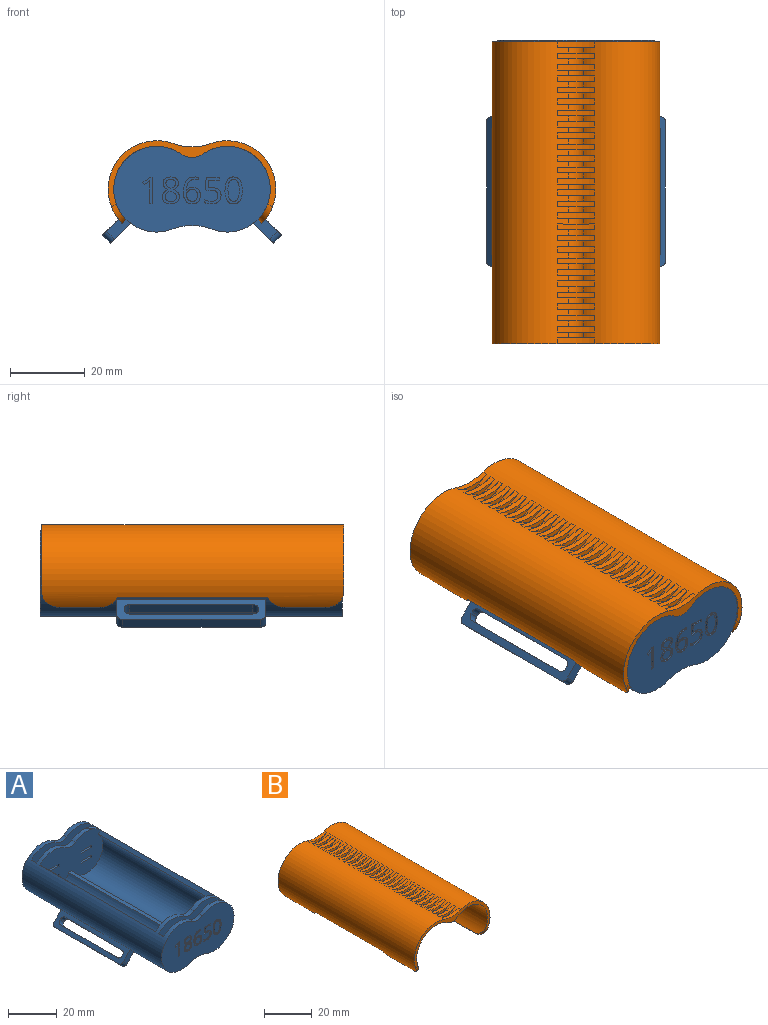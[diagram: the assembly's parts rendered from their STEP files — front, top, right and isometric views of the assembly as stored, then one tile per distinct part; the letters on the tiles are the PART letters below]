
ASSEMBLY  parts=2 mates=1
PART A: 205 faces, bbox 48x81x26 mm
  f0: plane 42x23mm, normal (0,-1,0), area 718.4mm2, adj f3,f9,f52,f88,f89,f90,f91,f92
  f1: plane 40x5.37mm, normal (0.71,0,-0.71), area 175.3mm2, adj f3,f23,f24,f39,f40,f41,f42,f43
  f2: plane 40x5.37mm, normal (-0.71,0,0.71), area 175.3mm2, adj f3,f23,f24,f39,f40,f41,f42,f43
  f3: cylinder r=11.5mm len=81mm, axis (0,1,0), area 2543.9mm2, adj f0,f1,f2,f4,f5,f8,f9,f20
  f4: plane 38x21mm, normal (0,1,0), area 630.6mm2, adj f3,f10,f11,f12,f13,f14,f15,f16
  f5: plane 38x21mm, normal (0,-1,0), area 630.6mm2, adj f3,f6,f7,f8,f10,f11,f12,f13
  f6: plane 67x1.77mm, normal (0,0,1), area 118.3mm2, adj f5,f7,f26,f53
  f7: cylinder r=9.5mm len=67mm, axis (0,1,0), area 2222.9mm2, adj f5,f6,f8,f26
  f8: plane 67x1.41mm, normal (0.71,0,0.71), area 134mm2, adj f3,f5,f7,f26
  f9: cylinder r=15mm len=81mm, axis (0,1,0), area 891mm2, adj f0,f3,f22,f52
  f10: plane 2x1mm, normal (-1,0,0), area 2mm2, adj f4,f5,f11,f13
  f11: plane 6x2mm, normal (0,0,1), area 12mm2, adj f4,f5,f10,f12
  f12: plane 2x1mm, normal (1,0,0), area 2mm2, adj f4,f5,f11,f13
  f13: plane 6x2mm, normal (0,0,-1), area 12mm2, adj f4,f5,f10,f12
  f14: plane 6x2mm, normal (0,0,1), area 12mm2, adj f4,f5,f15,f17
  f15: plane 2x1mm, normal (1,0,0), area 2mm2, adj f4,f5,f14,f16
  f16: plane 6x2mm, normal (0,0,-1), area 12mm2, adj f4,f5,f15,f17
  f17: plane 2x1mm, normal (-1,0,0), area 2mm2, adj f4,f5,f14,f16
  f18: plane 3x1.77mm, normal (0,0,1), area 5.3mm2, adj f4,f19,f21,f63
  f19: cylinder r=9.5mm len=18.12mm, axis (0,-1,0), area 99.5mm2, adj f4,f18,f20,f21
  f20: plane 3x1.41mm, normal (0.71,0,0.71), area 6mm2, adj f3,f4,f19,f21
  f21: plane 38x21mm, normal (0,-1,0), area 641.7mm2, adj f3,f18,f19,f20,f52,f63,f64,f197
  f22: plane 42x23mm, normal (0,1,0), area 797.6mm2, adj f3,f9,f52,f197,f198,f199,f200,f203
  f23: plane 37x2.14mm, normal (-0.71,0,-0.71), area 111.8mm2, adj f1,f2,f48,f49
  f24: plane 6.44x6.44mm, normal (0,1,0), area 18.2mm2, adj f1,f2,f3,f49
  f25: plane 38x21mm, normal (0,-1,0), area 630.6mm2, adj f3,f27,f28,f29,f30,f31,f32,f33
  f26: plane 38x21mm, normal (0,1,0), area 630.6mm2, adj f3,f6,f7,f8,f27,f28,f29,f30
  f27: plane 2x1mm, normal (-1,0,0), area 2mm2, adj f25,f26,f28,f30
  f28: plane 6x2mm, normal (0,0,1), area 12mm2, adj f25,f26,f27,f29
  f29: plane 2x1mm, normal (1,0,0), area 2mm2, adj f25,f26,f28,f30
  f30: plane 6x2mm, normal (0,0,-1), area 12mm2, adj f25,f26,f27,f29
  f31: plane 6x2mm, normal (0,0,1), area 12mm2, adj f25,f26,f32,f34
  f32: plane 2x1mm, normal (1,0,0), area 2mm2, adj f25,f26,f31,f33
  f33: plane 6x2mm, normal (0,0,-1), area 12mm2, adj f25,f26,f32,f34
  f34: plane 2x1mm, normal (-1,0,0), area 2mm2, adj f25,f26,f31,f33
  f35: plane 3x1.77mm, normal (0,0,1), area 5.3mm2, adj f25,f36,f38,f75
  f36: cylinder r=9.5mm len=18.12mm, axis (0,1,0), area 99.5mm2, adj f25,f35,f37,f38
  f37: plane 3x1.41mm, normal (0.71,0,0.71), area 6mm2, adj f3,f25,f36,f38
  f38: plane 38x21mm, normal (0,1,0), area 654.6mm2, adj f3,f35,f36,f37,f52,f75,f76,f202
  f39: plane 6.44x6.44mm, normal (0,-1,0), area 18.2mm2, adj f1,f2,f3,f48
  f40: plane 2.55x2.55mm, normal (0,1,0), area 1.8mm2, adj f1,f2,f44,f47
  f41: plane 33x2.14mm, normal (-0.71,0,-0.71), area 99.7mm2, adj f1,f2,f44,f45
  f42: plane 2.55x2.55mm, normal (0,-1,0), area 1.8mm2, adj f1,f2,f45,f46
  f43: plane 33x2.14mm, normal (0.71,0,0.71), area 99.7mm2, adj f1,f2,f46,f47
  f44: cylinder r=1.5mm len=3.2mm, axis (0.71,0,-0.71), area 7.1mm2, adj f1,f2,f40,f41
  f45: cylinder r=1.5mm len=3.2mm, axis (-0.71,0,0.71), area 7.1mm2, adj f1,f2,f41,f42
  f46: cylinder r=1.5mm len=3.2mm, axis (0.71,0,-0.71), area 7.1mm2, adj f1,f2,f42,f43
  f47: cylinder r=1.5mm len=3.2mm, axis (-0.71,0,0.71), area 7.1mm2, adj f1,f2,f40,f43
  f48: cylinder r=1.5mm len=3.2mm, axis (-0.71,0,0.71), area 7.1mm2, adj f1,f2,f23,f39
  f49: cylinder r=1.5mm len=3.2mm, axis (-0.71,0,0.71), area 7.1mm2, adj f1,f2,f23,f24
  f50: plane 40x5.37mm, normal (-0.71,0,-0.71), area 175.3mm2, adj f52,f65,f66,f77,f78,f79,f80,f81
  f51: plane 40x5.37mm, normal (0.71,0,0.71), area 175.3mm2, adj f52,f65,f66,f77,f78,f79,f80,f81
  f52: cylinder r=11.5mm len=81mm, axis (0,1,0), area 2543.9mm2, adj f0,f4,f5,f9,f21,f22,f25,f26
  f53: cylinder r=9.5mm len=67mm, axis (0,1,0), area 2222.9mm2, adj f5,f6,f26,f54
  f54: plane 67x1.41mm, normal (-0.71,0,0.71), area 134mm2, adj f5,f26,f52,f53
  f55: plane 2x1mm, normal (1,0,0), area 2mm2, adj f4,f5,f56,f58
  f56: plane 6x2mm, normal (0,0,1), area 12mm2, adj f4,f5,f55,f57
  f57: plane 2x1mm, normal (-1,0,0), area 2mm2, adj f4,f5,f56,f58
  f58: plane 6x2mm, normal (0,0,-1), area 12mm2, adj f4,f5,f55,f57
  f59: plane 6x2mm, normal (0,0,1), area 12mm2, adj f4,f5,f60,f62
  f60: plane 2x1mm, normal (-1,0,0), area 2mm2, adj f4,f5,f59,f61
  f61: plane 6x2mm, normal (0,0,-1), area 12mm2, adj f4,f5,f60,f62
  f62: plane 2x1mm, normal (1,0,0), area 2mm2, adj f4,f5,f59,f61
  f63: cylinder r=9.5mm len=18.12mm, axis (0,-1,0), area 99.5mm2, adj f4,f18,f21,f64
  f64: plane 3x1.41mm, normal (-0.71,0,0.71), area 6mm2, adj f4,f21,f52,f63
  f65: plane 37x2.14mm, normal (0.71,0,-0.71), area 111.8mm2, adj f50,f51,f86,f87
  f66: plane 6.44x6.44mm, normal (0,1,0), area 18.2mm2, adj f50,f51,f52,f87
  f67: plane 2x1mm, normal (1,0,0), area 2mm2, adj f25,f26,f68,f70
  f68: plane 6x2mm, normal (0,0,1), area 12mm2, adj f25,f26,f67,f69
  f69: plane 2x1mm, normal (-1,0,0), area 2mm2, adj f25,f26,f68,f70
  f70: plane 6x2mm, normal (0,0,-1), area 12mm2, adj f25,f26,f67,f69
  f71: plane 6x2mm, normal (0,0,1), area 12mm2, adj f25,f26,f72,f74
  f72: plane 2x1mm, normal (-1,0,0), area 2mm2, adj f25,f26,f71,f73
  f73: plane 6x2mm, normal (0,0,-1), area 12mm2, adj f25,f26,f72,f74
  f74: plane 2x1mm, normal (1,0,0), area 2mm2, adj f25,f26,f71,f73
  f75: cylinder r=9.5mm len=18.12mm, axis (0,1,0), area 99.5mm2, adj f25,f35,f38,f76
  f76: plane 3x1.41mm, normal (-0.71,0,0.71), area 6mm2, adj f25,f38,f52,f75
  f77: plane 6.44x6.44mm, normal (0,-1,0), area 18.2mm2, adj f50,f51,f52,f86
  f78: plane 2.55x2.55mm, normal (0,1,0), area 1.8mm2, adj f50,f51,f82,f85
  f79: plane 33x2.14mm, normal (0.71,0,-0.71), area 99.7mm2, adj f50,f51,f82,f83
  f80: plane 2.55x2.55mm, normal (0,-1,0), area 1.8mm2, adj f50,f51,f83,f84
  f81: plane 33x2.14mm, normal (-0.71,0,0.71), area 99.7mm2, adj f50,f51,f84,f85
  f82: cylinder r=1.5mm len=3.2mm, axis (-0.71,0,-0.71), area 7.1mm2, adj f50,f51,f78,f79
  f83: cylinder r=1.5mm len=3.2mm, axis (0.71,0,0.71), area 7.1mm2, adj f50,f51,f79,f80
  f84: cylinder r=1.5mm len=3.2mm, axis (-0.71,0,-0.71), area 7.1mm2, adj f50,f51,f80,f81
  f85: cylinder r=1.5mm len=3.2mm, axis (0.71,0,0.71), area 7.1mm2, adj f50,f51,f78,f81
  f86: cylinder r=1.5mm len=3.2mm, axis (0.71,0,0.71), area 7.1mm2, adj f50,f51,f65,f77
  f87: cylinder r=1.5mm len=3.2mm, axis (0.71,0,0.71), area 7.1mm2, adj f50,f51,f65,f66
  f88: extruded ~1.1x0.5mm, area 0.6mm2, adj f0,f89,f106,f107
  f89: plane 2.11x0.5mm, normal (-1,0,0.08), area 1.1mm2, adj f0,f88,f90,f107
  f90: plane 2.81x0.5mm, normal (0,0,1), area 1.4mm2, adj f0,f89,f91,f107
  f91: plane 0.73x0.5mm, normal (-1,0,0), area 0.4mm2, adj f0,f90,f92,f107
  f92: plane 3.49x0.5mm, normal (0,0,-1), area 1.7mm2, adj f0,f91,f93,f107
  f93: plane 3.28x0.5mm, normal (1,0,-0.08), area 1.6mm2, adj f0,f92,f94,f107
  f94: plane 0.5x0.41mm, normal (0.54,0,0.84), area 0.2mm2, adj f0,f93,f95,f107
  f95: extruded ~1.22x0.5mm, area 0.6mm2, adj f0,f94,f96,f107
  f96: extruded ~1.8x1.47mm, area 1.3mm2, adj f0,f95,f97,f107
  f97: extruded ~1.15x0.5mm, area 0.6mm2, adj f0,f96,f98,f107
  f98: extruded ~1.31x0.5mm, area 0.7mm2, adj f0,f97,f99,f107
  f99: extruded ~0.98x0.5mm, area 0.5mm2, adj f0,f98,f100,f107
  f100: extruded ~0.83x0.5mm, area 0.5mm2, adj f0,f99,f101,f107
  f101: plane 0.77x0.5mm, normal (1,0,0), area 0.4mm2, adj f0,f100,f102,f107
  f102: extruded ~1.81x0.5mm, area 0.9mm2, adj f0,f101,f103,f107
  f103: extruded ~1.91x0.62mm, area 1mm2, adj f0,f102,f104,f107
  f104: extruded ~1.71x0.69mm, area 1mm2, adj f0,f103,f105,f107
  f105: extruded ~1.5x0.64mm, area 0.8mm2, adj f0,f104,f106,f107
  f106: extruded ~1.74x0.55mm, area 0.9mm2, adj f0,f88,f105,f107
  f107: plane 7.11x4.41mm, normal (0,-1,0), area 11.4mm2, adj f88,f89,f90,f91,f92,f93,f94,f95
  f108: extruded ~2.28x0.64mm, area 1.2mm2, adj f0,f109,f132,f133
  f109: extruded ~1.73x0.82mm, area 1mm2, adj f0,f108,f110,f133
  f110: extruded ~1.61x0.63mm, area 0.9mm2, adj f0,f109,f111,f133
  f111: extruded ~1.72x0.6mm, area 0.9mm2, adj f0,f110,f112,f133
  f112: extruded ~1.55x0.54mm, area 0.8mm2, adj f0,f111,f113,f133
  f113: extruded ~1.49x0.57mm, area 0.8mm2, adj f0,f112,f114,f133
  f114: extruded ~1.67x0.83mm, area 1mm2, adj f0,f113,f115,f133
  f115: plane 0.5x0.06mm, normal (0,0,-1), area 0mm2, adj f0,f114,f116,f133
  f116: extruded ~2.21x0.65mm, area 1.2mm2, adj f0,f115,f117,f133
  f117: extruded ~1.72x0.7mm, area 1mm2, adj f0,f116,f118,f133
  f118: extruded ~0.84x0.5mm, area 0.4mm2, adj f0,f117,f119,f133
  f119: plane 0.69x0.5mm, normal (-1,0,0), area 0.3mm2, adj f0,f118,f120,f133
  f120: extruded ~0.85x0.5mm, area 0.4mm2, adj f0,f119,f121,f133
  f121: extruded ~2.38x1.02mm, area 1.3mm2, adj f0,f120,f132,f133
  f122: extruded ~0.8x0.5mm, area 0.4mm2, adj f123,f131,f133,f134
  f123: extruded ~0.68x0.54mm, area 0.4mm2, adj f122,f124,f133,f134
  f124: extruded ~0.92x0.5mm, area 0.5mm2, adj f123,f125,f133,f134
  f125: extruded ~0.65x0.5mm, area 0.3mm2, adj f124,f126,f133,f134
  f126: extruded ~0.57x0.5mm, area 0.4mm2, adj f125,f127,f133,f134
  f127: extruded ~0.79x0.5mm, area 0.4mm2, adj f126,f128,f133,f134
  f128: extruded ~1.05x0.5mm, area 0.6mm2, adj f127,f129,f133,f134
  f129: extruded ~1.09x0.5mm, area 0.6mm2, adj f128,f130,f133,f134
  f130: extruded ~1.24x0.5mm, area 0.7mm2, adj f129,f131,f133,f134
  f131: extruded ~1.06x0.5mm, area 0.6mm2, adj f122,f130,f133,f134
  f132: extruded ~3.09x0.8mm, area 1.6mm2, adj f0,f108,f121,f133
  f133: plane 7.21x4.58mm, normal (0,-1,0), area 12.7mm2, adj f108,f109,f110,f111,f112,f113,f114,f115
  f134: plane 3.16x2.97mm, normal (0,-1,0), area 7.6mm2, adj f122,f123,f124,f125,f126,f127,f128,f129
  f135: extruded ~2.68x0.59mm, area 1.4mm2, adj f0,f136,f150,f151
  f136: extruded ~1.73x0.93mm, area 1mm2, adj f0,f135,f137,f151
  f137: extruded ~1.74x0.89mm, area 1mm2, adj f0,f136,f138,f151
  f138: extruded ~2.72x0.57mm, area 1.4mm2, adj f0,f137,f139,f151
  f139: extruded ~2.69x0.59mm, area 1.4mm2, adj f0,f138,f140,f151
  f140: extruded ~1.72x0.92mm, area 1mm2, adj f0,f139,f141,f151
  f141: extruded ~1.75x0.9mm, area 1mm2, adj f0,f140,f150,f151
  f142: extruded ~2.22x0.5mm, area 1.1mm2, adj f143,f149,f151,f152
  f143: extruded ~1.15x0.69mm, area 0.7mm2, adj f142,f144,f151,f152
  f144: extruded ~1.15x0.7mm, area 0.7mm2, adj f143,f145,f151,f152
  f145: extruded ~2.21x0.5mm, area 1.1mm2, adj f144,f146,f151,f152
  f146: extruded ~2.22x0.5mm, area 1.1mm2, adj f145,f147,f151,f152
  f147: extruded ~1.15x0.71mm, area 0.7mm2, adj f146,f148,f151,f152
  f148: extruded ~1.15x0.7mm, area 0.7mm2, adj f147,f149,f151,f152
  f149: extruded ~2.23x0.5mm, area 1.1mm2, adj f142,f148,f151,f152
  f150: extruded ~2.72x0.57mm, area 1.4mm2, adj f0,f135,f141,f151
  f151: plane 7.22x4.64mm, normal (0,-1,0), area 13mm2, adj f135,f136,f137,f138,f139,f140,f141,f142
  f152: plane 5.84x3.02mm, normal (0,-1,0), area 14.9mm2, adj f142,f143,f144,f145,f146,f147,f148,f149
  f153: extruded ~1.51x0.5mm, area 0.8mm2, adj f0,f154,f183,f184
  f154: extruded ~1.22x0.56mm, area 0.7mm2, adj f0,f153,f155,f184
  f155: extruded ~0.97x0.5mm, area 0.5mm2, adj f0,f154,f156,f184
  f156: extruded ~0.95x0.81mm, area 0.6mm2, adj f0,f155,f157,f184
  f157: extruded ~1.88x1.47mm, area 1.3mm2, adj f0,f156,f158,f184
  f158: extruded ~1.39x0.6mm, area 0.8mm2, adj f0,f157,f159,f184
  f159: extruded ~1.73x0.5mm, area 0.9mm2, adj f0,f158,f160,f184
  f160: extruded ~1.67x0.52mm, area 0.9mm2, adj f0,f159,f161,f184
  f161: extruded ~1.39x0.61mm, area 0.8mm2, adj f0,f160,f162,f184
  f162: extruded ~1.04x0.5mm, area 0.6mm2, adj f0,f161,f163,f184
  f163: extruded ~1.21x0.86mm, area 0.7mm2, adj f0,f162,f164,f184
  f164: extruded ~1.03x0.78mm, area 0.6mm2, adj f0,f163,f165,f184
  f165: extruded ~0.95x0.5mm, area 0.5mm2, adj f0,f164,f166,f184
  f166: extruded ~1.23x0.56mm, area 0.7mm2, adj f0,f165,f183,f184
  f167: extruded ~0.89x0.5mm, area 0.5mm2, adj f168,f181,f184,f186
  f168: extruded ~1.04x0.68mm, area 0.6mm2, adj f167,f169,f184,f186
  f169: extruded ~1.3x0.7mm, area 0.7mm2, adj f168,f170,f184,f186
  f170: extruded ~0.83x0.5mm, area 0.5mm2, adj f169,f171,f184,f186
  f171: extruded ~0.92x0.5mm, area 0.5mm2, adj f170,f172,f184,f186
  f172: extruded ~1.11x0.5mm, area 0.6mm2, adj f171,f173,f184,f186
  f173: extruded ~1.12x0.5mm, area 0.6mm2, adj f172,f181,f184,f186
  f174: extruded ~0.96x0.5mm, area 0.5mm2, adj f175,f182,f184,f185
  f175: extruded ~0.77x0.5mm, area 0.4mm2, adj f174,f176,f184,f185
  f176: extruded ~0.77x0.5mm, area 0.4mm2, adj f175,f177,f184,f185
  f177: extruded ~0.97x0.62mm, area 0.6mm2, adj f176,f178,f184,f185
  f178: extruded ~1.05x0.63mm, area 0.6mm2, adj f177,f179,f184,f185
  f179: extruded ~0.76x0.5mm, area 0.4mm2, adj f178,f180,f184,f185
  f180: extruded ~0.77x0.5mm, area 0.4mm2, adj f179,f182,f184,f185
  f181: extruded ~0.9x0.5mm, area 0.5mm2, adj f167,f173,f184,f186
  f182: extruded ~0.94x0.5mm, area 0.5mm2, adj f174,f180,f184,f185
  f183: extruded ~1.52x0.5mm, area 0.8mm2, adj f0,f153,f166,f184
  f184: plane 7.21x4.61mm, normal (0,-1,0), area 14.6mm2, adj f153,f154,f155,f156,f157,f158,f159,f160
  f185: plane 2.59x2.45mm, normal (0,-1,0), area 4.8mm2, adj f174,f175,f176,f177,f178,f179,f180,f182
  f186: plane 3.04x2.79mm, normal (0,-1,0), area 6.4mm2, adj f167,f168,f169,f170,f171,f172,f173,f181
  f187: plane 7.01x0.5mm, normal (-1,0,0), area 3.5mm2, adj f0,f188,f195,f196
  f188: plane 0.67x0.5mm, normal (0,0,-1), area 0.3mm2, adj f0,f187,f189,f196
  f189: plane 1.86x1.44mm, normal (0.61,0,-0.79), area 1.2mm2, adj f0,f188,f190,f196
  f190: plane 0.55x0.5mm, normal (0.79,0,0.61), area 0.3mm2, adj f0,f189,f191,f196
  f191: extruded ~1.14x0.94mm, area 0.7mm2, adj f0,f190,f192,f196
  f192: extruded ~0.5x0.23mm, area 0.2mm2, adj f0,f191,f193,f196
  f193: extruded ~1.18x0.5mm, area 0.6mm2, adj f0,f192,f194,f196
  f194: plane 5x0.5mm, normal (1,0,0), area 2.5mm2, adj f0,f193,f195,f196
  f195: plane 0.78x0.5mm, normal (0,0,1), area 0.4mm2, adj f0,f187,f194,f196
  f196: plane 7.01x2.53mm, normal (0,-1,0), area 6.7mm2, adj f187,f188,f189,f190,f191,f192,f193,f194
  f197: cylinder r=1.5mm len=3mm, axis (0,1,0), area 10.4mm2, adj f21,f22,f199,f200
  f198: cylinder r=1.5mm len=3mm, axis (0,1,0), area 10.4mm2, adj f21,f22,f199,f200
  f199: cylinder r=5mm len=2mm, axis (0,1,0), area 3.1mm2, adj f21,f22,f197,f198
  f200: cylinder r=5mm len=2mm, axis (0,1,0), area 3.1mm2, adj f21,f22,f197,f198
  f201: cylinder r=5mm len=5.76mm, axis (0,-1,0), area 12.3mm2, adj f3,f25,f26,f52
  f202: cylinder r=5mm len=5.76mm, axis (0,-1,0), area 12.3mm2, adj f0,f3,f38,f52
  f203: cylinder r=5mm len=5.76mm, axis (0,1,0), area 12.3mm2, adj f3,f21,f22,f52
  f204: cylinder r=5mm len=5.76mm, axis (0,1,0), area 12.3mm2, adj f3,f4,f5,f52
PART B: 126 faces, bbox 45x81x23.1 mm
  f0: plane 10.6x1.06mm, normal (-0.71,0,-0.71), area 15.8mm2, adj f1,f34,f118,f121
  f1: cylinder r=13mm len=80.94mm, axis (0,1,0), area 2827.1mm2, adj f0,f2,f3,f4,f5,f6,f7,f8
  f2: cylinder r=3.5mm len=4.03mm, axis (0,1,0), area 6.7mm2, adj f1,f28,f113,f117
  f3: cylinder r=3.5mm len=4.03mm, axis (0,1,0), area 6.7mm2, adj f1,f28,f110,f114
  f4: cylinder r=3.5mm len=4.03mm, axis (0,1,0), area 6.7mm2, adj f1,f28,f107,f111
  f5: cylinder r=3.5mm len=4.03mm, axis (0,1,0), area 6.7mm2, adj f1,f28,f104,f108
  f6: cylinder r=3.5mm len=4.03mm, axis (0,1,0), area 6.7mm2, adj f1,f28,f101,f105
  f7: cylinder r=3.5mm len=4.03mm, axis (0,1,0), area 6.7mm2, adj f1,f28,f98,f102
  f8: cylinder r=3.5mm len=4.03mm, axis (0,1,0), area 6.7mm2, adj f1,f28,f95,f99
  f9: cylinder r=3.5mm len=4.03mm, axis (0,1,0), area 6.7mm2, adj f1,f28,f92,f96
  f10: cylinder r=3.5mm len=4.03mm, axis (0,1,0), area 6.7mm2, adj f1,f28,f89,f93
  f11: cylinder r=3.5mm len=4.03mm, axis (0,1,0), area 6.7mm2, adj f1,f28,f86,f90
  f12: cylinder r=3.5mm len=4.03mm, axis (0,1,0), area 6.7mm2, adj f1,f28,f83,f87
  f13: cylinder r=3.5mm len=4.03mm, axis (0,1,0), area 6.7mm2, adj f1,f28,f80,f84
  f14: cylinder r=3.5mm len=4.03mm, axis (0,1,0), area 6.7mm2, adj f1,f28,f77,f81
  f15: cylinder r=3.5mm len=4.03mm, axis (0,1,0), area 6.7mm2, adj f1,f28,f74,f78
  f16: cylinder r=3.5mm len=4.03mm, axis (0,1,0), area 6.7mm2, adj f1,f28,f71,f75
  f17: cylinder r=3.5mm len=4.03mm, axis (0,1,0), area 6.7mm2, adj f1,f28,f68,f72
  f18: cylinder r=3.5mm len=4.03mm, axis (0,1,0), area 6.7mm2, adj f1,f28,f65,f69
  f19: cylinder r=3.5mm len=4.03mm, axis (0,1,0), area 6.7mm2, adj f1,f28,f62,f66
  f20: cylinder r=3.5mm len=4.03mm, axis (0,1,0), area 6.7mm2, adj f1,f28,f59,f63
  f21: cylinder r=3.5mm len=4.03mm, axis (0,1,0), area 6.7mm2, adj f1,f28,f56,f60
  f22: cylinder r=3.5mm len=4.03mm, axis (0,1,0), area 6.7mm2, adj f1,f28,f53,f57
  f23: cylinder r=3.5mm len=4.03mm, axis (0,1,0), area 6.7mm2, adj f1,f28,f50,f54
  f24: cylinder r=3.5mm len=4.03mm, axis (0,1,0), area 6.7mm2, adj f1,f28,f47,f51
  f25: cylinder r=3.5mm len=4.03mm, axis (0,1,0), area 6.7mm2, adj f1,f28,f44,f48
  f26: cylinder r=3.5mm len=4.03mm, axis (0,1,0), area 6.7mm2, adj f1,f28,f41,f45
  f27: cylinder r=3.5mm len=4.03mm, axis (0,1,0), area 6.7mm2, adj f1,f28,f39,f42
  f28: cylinder r=13mm len=80.94mm, axis (0,1,0), area 2827.1mm2, adj f2,f3,f4,f5,f6,f7,f8,f9
  f29: cylinder r=11.5mm len=80.94mm, axis (0,1,0), area 2602.9mm2, adj f30,f31,f32,f33,f37,f116,f119,f120
  f30: cylinder r=5mm len=80.94mm, axis (0,1,0), area 496.6mm2, adj f29,f32,f34,f116
  f31: plane 10.66x1.06mm, normal (0.71,0,-0.71), area 15.9mm2, adj f28,f29,f124,f125
  f32: plane 45x17.95mm, normal (0,-1,0), area 108mm2, adj f1,f28,f29,f30,f34,f38,f123,f125
  f33: plane 40.42x1.32mm, normal (0.5,0,-0.87), area 60.6mm2, adj f28,f29,f120,f124
  f34: cylinder r=11.5mm len=80.94mm, axis (0,1,0), area 2602.9mm2, adj f0,f30,f32,f35,f36,f116,f118,f121
  f35: plane 10.66x1.06mm, normal (-0.71,0,-0.71), area 15.9mm2, adj f1,f34,f122,f123
  f36: plane 40.42x1.32mm, normal (-0.5,0,-0.87), area 60.6mm2, adj f1,f34,f121,f122
  f37: plane 10.6x1.06mm, normal (0.71,0,-0.71), area 15.8mm2, adj f28,f29,f119,f120
  f38: cylinder r=15mm len=10.18mm, axis (0,-1,0), area 15.6mm2, adj f1,f28,f32,f39
  f39: plane 10.18x2.24mm, normal (0,1,0), area 6.5mm2, adj f1,f27,f28,f38
  f40: cylinder r=15mm len=10.18mm, axis (0,-1,0), area 15.6mm2, adj f1,f28,f41,f42
  f41: plane 10.18x2.24mm, normal (0,1,0), area 6.5mm2, adj f1,f26,f28,f40
  f42: plane 10.18x2.24mm, normal (0,-1,0), area 6.5mm2, adj f1,f27,f28,f40
  f43: cylinder r=15mm len=10.18mm, axis (0,-1,0), area 15.6mm2, adj f1,f28,f44,f45
  f44: plane 10.18x2.24mm, normal (0,1,0), area 6.5mm2, adj f1,f25,f28,f43
  f45: plane 10.18x2.24mm, normal (0,-1,0), area 6.5mm2, adj f1,f26,f28,f43
  f46: cylinder r=15mm len=10.18mm, axis (0,-1,0), area 15.6mm2, adj f1,f28,f47,f48
  f47: plane 10.18x2.24mm, normal (0,1,0), area 6.5mm2, adj f1,f24,f28,f46
  f48: plane 10.18x2.24mm, normal (0,-1,0), area 6.5mm2, adj f1,f25,f28,f46
  f49: cylinder r=15mm len=10.18mm, axis (0,-1,0), area 15.6mm2, adj f1,f28,f50,f51
  f50: plane 10.18x2.24mm, normal (0,1,0), area 6.5mm2, adj f1,f23,f28,f49
  f51: plane 10.18x2.24mm, normal (0,-1,0), area 6.5mm2, adj f1,f24,f28,f49
  f52: cylinder r=15mm len=10.18mm, axis (0,-1,0), area 15.6mm2, adj f1,f28,f53,f54
  f53: plane 10.18x2.24mm, normal (0,1,0), area 6.5mm2, adj f1,f22,f28,f52
  f54: plane 10.18x2.24mm, normal (0,-1,0), area 6.5mm2, adj f1,f23,f28,f52
  f55: cylinder r=15mm len=10.18mm, axis (0,-1,0), area 15.6mm2, adj f1,f28,f56,f57
  f56: plane 10.18x2.24mm, normal (0,1,0), area 6.5mm2, adj f1,f21,f28,f55
  f57: plane 10.18x2.24mm, normal (0,-1,0), area 6.5mm2, adj f1,f22,f28,f55
  f58: cylinder r=15mm len=10.18mm, axis (0,-1,0), area 15.6mm2, adj f1,f28,f59,f60
  f59: plane 10.18x2.24mm, normal (0,1,0), area 6.5mm2, adj f1,f20,f28,f58
  f60: plane 10.18x2.24mm, normal (0,-1,0), area 6.5mm2, adj f1,f21,f28,f58
  f61: cylinder r=15mm len=10.18mm, axis (0,-1,0), area 15.6mm2, adj f1,f28,f62,f63
  f62: plane 10.18x2.24mm, normal (0,1,0), area 6.5mm2, adj f1,f19,f28,f61
  f63: plane 10.18x2.24mm, normal (0,-1,0), area 6.5mm2, adj f1,f20,f28,f61
  f64: cylinder r=15mm len=10.18mm, axis (0,-1,0), area 15.6mm2, adj f1,f28,f65,f66
  f65: plane 10.18x2.24mm, normal (0,1,0), area 6.5mm2, adj f1,f18,f28,f64
  f66: plane 10.18x2.24mm, normal (0,-1,0), area 6.5mm2, adj f1,f19,f28,f64
  f67: cylinder r=15mm len=10.18mm, axis (0,-1,0), area 15.6mm2, adj f1,f28,f68,f69
  f68: plane 10.18x2.24mm, normal (0,1,0), area 6.5mm2, adj f1,f17,f28,f67
  f69: plane 10.18x2.24mm, normal (0,-1,0), area 6.5mm2, adj f1,f18,f28,f67
  f70: cylinder r=15mm len=10.18mm, axis (0,-1,0), area 15.6mm2, adj f1,f28,f71,f72
  f71: plane 10.18x2.24mm, normal (0,1,0), area 6.5mm2, adj f1,f16,f28,f70
  f72: plane 10.18x2.24mm, normal (0,-1,0), area 6.5mm2, adj f1,f17,f28,f70
  f73: cylinder r=15mm len=10.18mm, axis (0,-1,0), area 15.6mm2, adj f1,f28,f74,f75
  f74: plane 10.18x2.24mm, normal (0,1,0), area 6.5mm2, adj f1,f15,f28,f73
  f75: plane 10.18x2.24mm, normal (0,-1,0), area 6.5mm2, adj f1,f16,f28,f73
  f76: cylinder r=15mm len=10.18mm, axis (0,-1,0), area 15.6mm2, adj f1,f28,f77,f78
  f77: plane 10.18x2.24mm, normal (0,1,0), area 6.5mm2, adj f1,f14,f28,f76
  f78: plane 10.18x2.24mm, normal (0,-1,0), area 6.5mm2, adj f1,f15,f28,f76
  f79: cylinder r=15mm len=10.18mm, axis (0,-1,0), area 15.6mm2, adj f1,f28,f80,f81
  f80: plane 10.18x2.24mm, normal (0,1,0), area 6.5mm2, adj f1,f13,f28,f79
  f81: plane 10.18x2.24mm, normal (0,-1,0), area 6.5mm2, adj f1,f14,f28,f79
  f82: cylinder r=15mm len=10.18mm, axis (0,-1,0), area 15.6mm2, adj f1,f28,f83,f84
  f83: plane 10.18x2.24mm, normal (0,1,0), area 6.5mm2, adj f1,f12,f28,f82
  f84: plane 10.18x2.24mm, normal (0,-1,0), area 6.5mm2, adj f1,f13,f28,f82
  f85: cylinder r=15mm len=10.18mm, axis (0,-1,0), area 15.6mm2, adj f1,f28,f86,f87
  f86: plane 10.18x2.24mm, normal (0,1,0), area 6.5mm2, adj f1,f11,f28,f85
  f87: plane 10.18x2.24mm, normal (0,-1,0), area 6.5mm2, adj f1,f12,f28,f85
  f88: cylinder r=15mm len=10.18mm, axis (0,-1,0), area 15.6mm2, adj f1,f28,f89,f90
  f89: plane 10.18x2.24mm, normal (0,1,0), area 6.5mm2, adj f1,f10,f28,f88
  f90: plane 10.18x2.24mm, normal (0,-1,0), area 6.5mm2, adj f1,f11,f28,f88
  f91: cylinder r=15mm len=10.18mm, axis (0,-1,0), area 15.6mm2, adj f1,f28,f92,f93
  f92: plane 10.18x2.24mm, normal (0,1,0), area 6.5mm2, adj f1,f9,f28,f91
  f93: plane 10.18x2.24mm, normal (0,-1,0), area 6.5mm2, adj f1,f10,f28,f91
  f94: cylinder r=15mm len=10.18mm, axis (0,-1,0), area 15.6mm2, adj f1,f28,f95,f96
  f95: plane 10.18x2.24mm, normal (0,1,0), area 6.5mm2, adj f1,f8,f28,f94
  f96: plane 10.18x2.24mm, normal (0,-1,0), area 6.5mm2, adj f1,f9,f28,f94
  f97: cylinder r=15mm len=10.18mm, axis (0,-1,0), area 15.6mm2, adj f1,f28,f98,f99
  f98: plane 10.18x2.24mm, normal (0,1,0), area 6.5mm2, adj f1,f7,f28,f97
  f99: plane 10.18x2.24mm, normal (0,-1,0), area 6.5mm2, adj f1,f8,f28,f97
  f100: cylinder r=15mm len=10.18mm, axis (0,-1,0), area 15.6mm2, adj f1,f28,f101,f102
  f101: plane 10.18x2.24mm, normal (0,1,0), area 6.5mm2, adj f1,f6,f28,f100
  f102: plane 10.18x2.24mm, normal (0,-1,0), area 6.5mm2, adj f1,f7,f28,f100
  f103: cylinder r=15mm len=10.18mm, axis (0,-1,0), area 15.6mm2, adj f1,f28,f104,f105
  f104: plane 10.18x2.24mm, normal (0,1,0), area 6.5mm2, adj f1,f5,f28,f103
  f105: plane 10.18x2.24mm, normal (0,-1,0), area 6.5mm2, adj f1,f6,f28,f103
  f106: cylinder r=15mm len=10.18mm, axis (0,-1,0), area 15.6mm2, adj f1,f28,f107,f108
  f107: plane 10.18x2.24mm, normal (0,1,0), area 6.5mm2, adj f1,f4,f28,f106
  f108: plane 10.18x2.24mm, normal (0,-1,0), area 6.5mm2, adj f1,f5,f28,f106
  f109: cylinder r=15mm len=10.18mm, axis (0,-1,0), area 15.6mm2, adj f1,f28,f110,f111
  f110: plane 10.18x2.24mm, normal (0,1,0), area 6.5mm2, adj f1,f3,f28,f109
  f111: plane 10.18x2.24mm, normal (0,-1,0), area 6.5mm2, adj f1,f4,f28,f109
  f112: cylinder r=15mm len=10.18mm, axis (0,-1,0), area 15.6mm2, adj f1,f28,f113,f114
  f113: plane 10.18x2.24mm, normal (0,1,0), area 6.5mm2, adj f1,f2,f28,f112
  f114: plane 10.18x2.24mm, normal (0,-1,0), area 6.5mm2, adj f1,f3,f28,f112
  f115: cylinder r=15mm len=10.18mm, axis (0,-1,0), area 15.6mm2, adj f1,f28,f116,f117
  f116: plane 45x17.95mm, normal (0,1,0), area 108mm2, adj f1,f28,f29,f30,f34,f115,f118,f119
  f117: plane 10.18x2.24mm, normal (0,-1,0), area 6.5mm2, adj f1,f2,f28,f115
  f118: cylinder r=5mm len=5.41mm, axis (-0.71,0,0.71), area 12.3mm2, adj f0,f1,f34,f116
  f119: cylinder r=5mm len=5.41mm, axis (0.71,0,0.71), area 12.3mm2, adj f28,f29,f37,f116
  f120: bspline ~4.78x4.52mm, area 9mm2, adj f28,f29,f33,f37
  f121: bspline ~6.31x4.98mm, area 8.9mm2, adj f0,f1,f34,f36
  f122: bspline ~4.78x4.52mm, area 9mm2, adj f1,f34,f35,f36
  f123: cylinder r=5mm len=5.41mm, axis (0.71,0,-0.71), area 12.3mm2, adj f1,f32,f34,f35
  f124: bspline ~6.31x4.98mm, area 8.9mm2, adj f28,f29,f31,f33
  f125: cylinder r=5mm len=5.41mm, axis (-0.71,0,-0.71), area 12.3mm2, adj f28,f29,f31,f32
PLACE A t=(0,-7,24.74)mm
PLACE B t=(0,-40.81,24.74)mm
MATE slider B.f2 <-> A.f201  axis (0,-1,0) through (0,-81.31,38.23)mm
